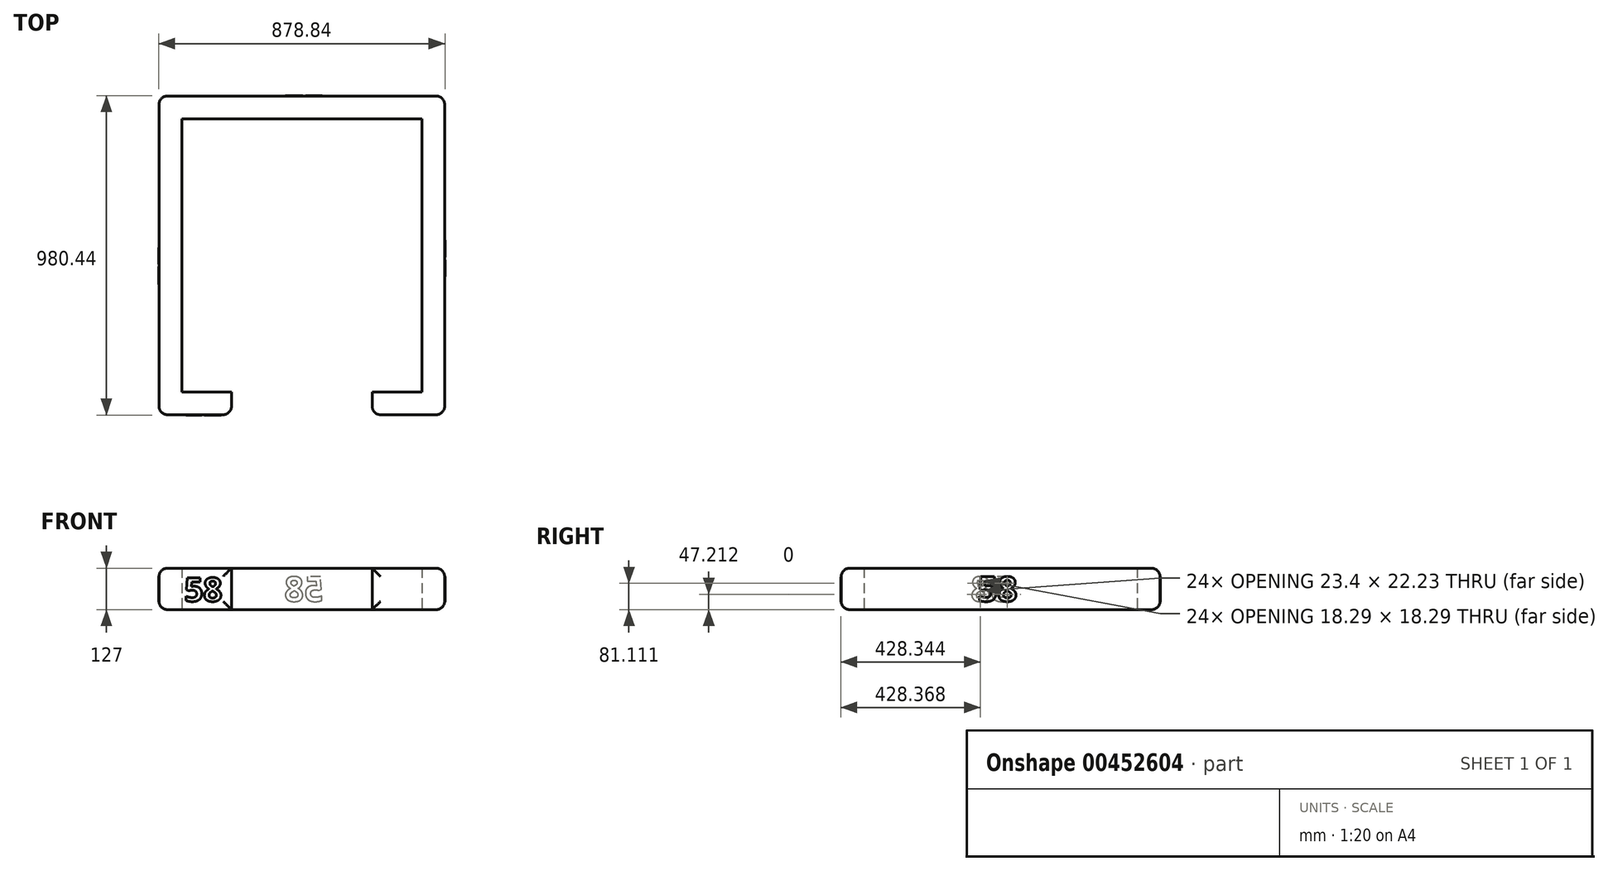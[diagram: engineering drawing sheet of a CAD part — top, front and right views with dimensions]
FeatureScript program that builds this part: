
annotation { "Feature Type Name" : "Feature", "Feature Type Description" : "" }
export const myFeature = defineFeature(function(context is Context, id is Id, definition is map)
    precondition{}
    {
        {
            var Q0;
            Q0=qCreatedBy(makeId("Top.planeOp"),FACE);
            var sketch = newSketch(context, id + "F0", { "sketchPlane" : qUnion([Q0])});
            skLineSegment(sketch, "E0.bottom", {"start": v(368.3, 419.1) * mm, "end": v(-368.3, 419.1) * mm});
            skLineSegment(sketch, "E0.top", {"start": v(368.3, -419.1) * mm, "end": v(215.9, -419.1) * mm});
            skLineSegment(sketch, "E0.left", {"start": v(368.3, 419.1) * mm, "end": v(368.3, -419.1) * mm});
            skLineSegment(sketch, "E0.right", {"start": v(-368.3, 419.1) * mm, "end": v(-368.3, -419.1) * mm});
            skPoint(sketch, "E0.middle", {"position": v(0, 0) * mm});
            skLineSegment(sketch, "E1.0", {"start": v(-438.15, 488.95) * mm, "end": v(-438.15, -488.95) * mm});
            skLineSegment(sketch, "E1.1", {"start": v(438.15, 488.95) * mm, "end": v(-438.15, 488.95) * mm});
            skLineSegment(sketch, "E1.2", {"start": v(438.15, 488.95) * mm, "end": v(438.15, -488.95) * mm});
            skLineSegment(sketch, "E1.3", {"start": v(438.15, -488.95) * mm, "end": v(215.9, -488.95) * mm});
            skLineSegment(sketch, "E2", {"start": v(-215.9, -488.95) * mm, "end": v(-215.9, -419.1) * mm});
            skLineSegment(sketch, "E3", {"start": v(215.9, -488.95) * mm, "end": v(215.9, -419.1) * mm});
            skLineSegment(sketch, "E4.trimOffspring", {"start": v(-215.9, -419.1) * mm, "end": v(-368.3, -419.1) * mm});
            skLineSegment(sketch, "E5.trimOffspring", {"start": v(-215.9, -488.95) * mm, "end": v(-438.15, -488.95) * mm});
            skSolve(sketch);
        }
        {
            var Q0;
            Q0=makeQuery(id+"F0.imprint","IMPRINT",FACE,{"disambiguationData":[TD([[makeQuery(id+"F0.imprint","IMPRINT",EDGE,{"derivedFrom":sQuery(id+"F0.wireOp",EDGE,"E0.bottom")}),-1.0]])]});
            extrude(context, id + "F1", {"entities" : qUnion([Q0]), "depth" : 127 * mm});
        }
        {
            var Q0;
            Q0=makeQuery(id+"F1.opExtrude","CAP_EDGE",EDGE,{"disambiguationData":[OSD([sQuery(id+"F0.wireOp",EDGE,"E1.2")])],"isStart":false});
            var Q1;
            Q1=makeQuery(id+"F1.opExtrude","CAP_EDGE",EDGE,{"disambiguationData":[OSD([sQuery(id+"F0.wireOp",EDGE,"E1.3")])],"isStart":false});
            var Q2;
            Q2=makeQuery(id+"F1.opExtrude","CAP_EDGE",EDGE,{"disambiguationData":[OSD([sQuery(id+"F0.wireOp",EDGE,"E1.1")])],"isStart":false});
            var Q3;
            Q3=makeQuery(id+"F1.opExtrude","CAP_EDGE",EDGE,{"disambiguationData":[OSD([sQuery(id+"F0.wireOp",EDGE,"E1.0")])],"isStart":false});
            var Q4;
            Q4=makeQuery(id+"F1.opExtrude","CAP_EDGE",EDGE,{"disambiguationData":[OSD([sQuery(id+"F0.wireOp",EDGE,"E5.trimOffspring")])],"isStart":false});
            var Q5;
            Q5=makeQuery(id+"F1.opExtrude","SWEPT_EDGE",EDGE,{"disambiguationData":[OSD([sQuery(id+"F0.wireOp",EDGE,"E2"),sQuery(id+"F0.wireOp",EDGE,"E5.trimOffspring")])]});
            var Q6;
            Q6=makeQuery(id+"F1.opExtrude","CAP_EDGE",EDGE,{"disambiguationData":[OSD([sQuery(id+"F0.wireOp",EDGE,"E5.trimOffspring")])],"isStart":true});
            var Q7;
            Q7=makeQuery(id+"F1.opExtrude","CAP_EDGE",EDGE,{"disambiguationData":[OSD([sQuery(id+"F0.wireOp",EDGE,"E1.0")])],"isStart":true});
            var Q8;
            Q8=makeQuery(id+"F1.opExtrude","CAP_EDGE",EDGE,{"disambiguationData":[OSD([sQuery(id+"F0.wireOp",EDGE,"E1.1")])],"isStart":true});
            var Q9;
            Q9=makeQuery(id+"F1.opExtrude","SWEPT_EDGE",EDGE,{"disambiguationData":[OSD([sQuery(id+"F0.wireOp",EDGE,"E1.0"),sQuery(id+"F0.wireOp",EDGE,"E1.1")])]});
            var Q10;
            Q10=makeQuery(id+"F1.opExtrude","SWEPT_EDGE",EDGE,{"disambiguationData":[OSD([sQuery(id+"F0.wireOp",EDGE,"E1.1"),sQuery(id+"F0.wireOp",EDGE,"E1.2")])]});
            var Q11;
            Q11=makeQuery(id+"F1.opExtrude","CAP_EDGE",EDGE,{"disambiguationData":[OSD([sQuery(id+"F0.wireOp",EDGE,"E1.2")])],"isStart":true});
            var Q12;
            Q12=makeQuery(id+"F1.opExtrude","SWEPT_EDGE",EDGE,{"disambiguationData":[OSD([sQuery(id+"F0.wireOp",EDGE,"E1.2"),sQuery(id+"F0.wireOp",EDGE,"E1.3")])]});
            var Q13;
            Q13=makeQuery(id+"F1.opExtrude","SWEPT_EDGE",EDGE,{"disambiguationData":[OSD([sQuery(id+"F0.wireOp",EDGE,"E1.3"),sQuery(id+"F0.wireOp",EDGE,"E3")])]});
            var Q14;
            Q14=makeQuery(id+"F1.opExtrude","CAP_EDGE",EDGE,{"disambiguationData":[OSD([sQuery(id+"F0.wireOp",EDGE,"E1.3")])],"isStart":true});
            fillet(context, id + "F2", {"entities" : qUnion([Q0, Q1, Q2, Q3, Q4, Q5, Q6, Q7, Q8, Q9, Q10, Q11, Q12, Q13, Q14]), "radius" : 25.4 * mm, "tangentPropagation" : true, "allowEdgeOverflow" : false});
        }
        {
            var Q0;
            Q0=makeQuery(id+"F1.opExtrude","SWEPT_FACE",FACE,{"disambiguationData":[OSD([sQuery(id+"F0.wireOp",EDGE,"E1.2")])]});
            var sketch = newSketch(context, id + "F3", { "sketchPlane" : qUnion([Q0])});
            skText(sketch, "E6", { "text": "58", "fontName": "OpenSans-Bold.ttf"});
            const initialGuessF3  = {"E6": [-0.06985, 0.0254, 1, 0, 0.0762]};
            skSetInitialGuess(sketch, initialGuessF3);
            skSolve(sketch);
        }
        {
            var Q0;
            Q0 = qSketchRegion(id + "F3", true);
            extrude(context, id + "F4", {"entities" : qUnion([Q0]), "depth" : 1.27 * mm});
        }
        {
            var Q0;
            Q0=makeQuery(id+"F1.opExtrude","SWEPT_FACE",FACE,{"disambiguationData":[OSD([sQuery(id+"F0.wireOp",EDGE,"E1.0")])]});
            var sketch = newSketch(context, id + "F5", { "sketchPlane" : qUnion([Q0])});
            skText(sketch, "E7", { "text": "58", "fontName": "OpenSans-Bold.ttf"});
            const initialGuessF5  = {"E7": [-0.02876, 0.0254, 1, 0, 0.0762]};
            skSetInitialGuess(sketch, initialGuessF5);
            skSolve(sketch);
        }
        {
            var Q0;
            Q0=makeQuery(id+"F1.opExtrude","SWEPT_FACE",FACE,{"disambiguationData":[OSD([sQuery(id+"F0.wireOp",EDGE,"E1.1")])]});
            var sketch = newSketch(context, id + "F6", { "sketchPlane" : qUnion([Q0])});
            skText(sketch, "E8", { "text": "58\n", "fontName": "OpenSans-Bold.ttf"});
            const initialGuessF6  = {"E8": [-0.06686, 0.0254, 1, 0, 0.0762]};
            skSetInitialGuess(sketch, initialGuessF6);
            skSolve(sketch);
        }
        {
            var Q0;
            Q0=makeQuery(id+"F1.opExtrude","SWEPT_EDGE",EDGE,{"disambiguationData":[OSD([sQuery(id+"F0.wireOp",EDGE,"E1.0"),sQuery(id+"F0.wireOp",EDGE,"E5.trimOffspring")])]});
            fillet(context, id + "F7", {"entities" : qUnion([Q0]), "radius" : 25.4 * mm, "tangentPropagation" : true, "allowEdgeOverflow" : false});
        }
        {
            var Q0;
            Q0=makeQuery(id+"F1.opExtrude","SWEPT_FACE",FACE,{"disambiguationData":[OSD([sQuery(id+"F0.wireOp",EDGE,"E5.trimOffspring")])]});
            var sketch = newSketch(context, id + "F8", { "sketchPlane" : qUnion([Q0])});
            skText(sketch, "E9", { "text": "58", "fontName": "OpenSans-Bold.ttf"});
            const initialGuessF8  = {"E9": [-0.36048, 0.0254, 1, 0, 0.07323]};
            skSetInitialGuess(sketch, initialGuessF8);
            skSolve(sketch);
        }
        {
            var Q0;
            Q0 = qSketchRegion(id + "F8", true);
            extrude(context, id + "F9", {"entities" : qUnion([Q0]), "depth" : 1.27 * mm});
        }
        {
            var Q0;
            Q0 = qSketchRegion(id + "F5", true);
            extrude(context, id + "F10", {"entities" : qUnion([Q0]), "depth" : 1.27 * mm});
        }
        {
            var Q0;
            Q0 = qSketchRegion(id + "F6", true);
            extrude(context, id + "F11", {"entities" : qUnion([Q0]), "depth" : 1.27 * mm});
        }
    });
